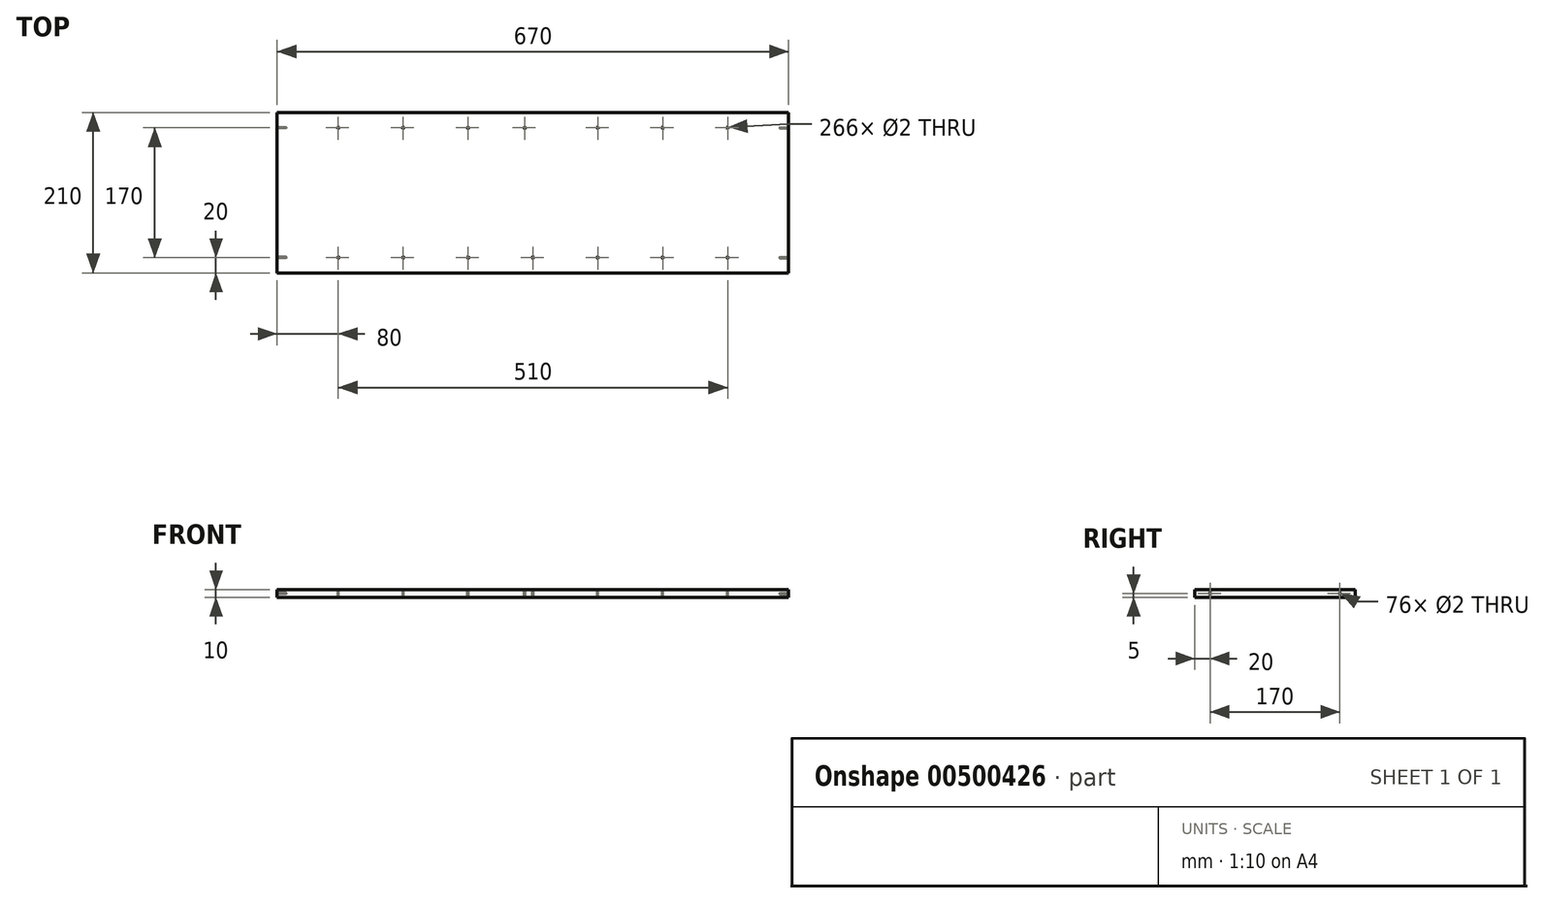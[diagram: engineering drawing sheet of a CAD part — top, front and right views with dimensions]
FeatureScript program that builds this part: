
annotation { "Feature Type Name" : "Feature", "Feature Type Description" : "" }
export const myFeature = defineFeature(function(context is Context, id is Id, definition is map)
    precondition{}
    {
        {
            var Q0;
            Q0=qCreatedBy(makeId("Top.planeOp"),FACE);
            var sketch = newSketch(context, id + "F0", { "sketchPlane" : qUnion([Q0])});
            skLineSegment(sketch, "E0.bottom", {"start": v(0, 0) * mm, "end": v(-670, 0) * mm});
            skLineSegment(sketch, "E0.top", {"start": v(0, -210) * mm, "end": v(-670, -210) * mm});
            skLineSegment(sketch, "E0.left", {"start": v(0, 0) * mm, "end": v(0, -210) * mm});
            skLineSegment(sketch, "E0.right", {"start": v(-670, 0) * mm, "end": v(-670, -210) * mm});
            skSolve(sketch);
        }
        {
            var Q0;
            Q0=makeQuery(id+"F0.imprint","IMPRINT",FACE,{"disambiguationData":[TD([[makeQuery(id+"F0.imprint","IMPRINT",EDGE,{"derivedFrom":sQuery(id+"F0.wireOp",EDGE,"E0.bottom")}),1.0]])]});
            extrude(context, id + "F1", {"entities" : qUnion([Q0]), "depth" : 10 * mm});
        }
        {
            var Q0;
            Q0=makeQuery(id+"F1.opExtrude","CAP_FACE",FACE,{"disambiguationData":[OSD([sQuery(id+"F0.wireOp",EDGE,"E0.bottom"),sQuery(id+"F0.wireOp",EDGE,"E0.top"),sQuery(id+"F0.wireOp",EDGE,"E0.left"),sQuery(id+"F0.wireOp",EDGE,"E0.right")])],"isStart":false});
            var sketch = newSketch(context, id + "F2", { "sketchPlane" : qUnion([Q0])});
            skPoint(sketch, "E1", {"position": v(-590, -190) * mm});
            skPoint(sketch, "E2", {"position": v(-505, -190) * mm});
            skPoint(sketch, "E3", {"position": v(-420, -190) * mm});
            skPoint(sketch, "E4", {"position": v(-335, -190) * mm});
            skPoint(sketch, "E5", {"position": v(-250, -190) * mm});
            skPoint(sketch, "E6", {"position": v(-165, -190) * mm});
            skPoint(sketch, "E7", {"position": v(-80, -190) * mm});
            skPoint(sketch, "E8", {"position": v(-590, -20) * mm});
            skPoint(sketch, "E9", {"position": v(-505, -20) * mm});
            skPoint(sketch, "E10", {"position": v(-420, -20) * mm});
            skPoint(sketch, "E11", {"position": v(-345.75, -20) * mm});
            skPoint(sketch, "E12", {"position": v(-250, -20) * mm});
            skPoint(sketch, "E13", {"position": v(-165, -20) * mm});
            skPoint(sketch, "E14", {"position": v(-80, -20) * mm});
            skSolve(sketch);
        }
        {
            var Q0;
            Q0=sQuery(id+"F2.wireOp",VERTEX,"E1");
            var Q1;
            Q1=sQuery(id+"F2.wireOp",VERTEX,"E2");
            var Q2;
            Q2=sQuery(id+"F2.wireOp",VERTEX,"E3");
            var Q3;
            Q3=sQuery(id+"F2.wireOp",VERTEX,"E4");
            var Q4;
            Q4=sQuery(id+"F2.wireOp",VERTEX,"E5");
            var Q5;
            Q5=sQuery(id+"F2.wireOp",VERTEX,"E6");
            var Q6;
            Q6=sQuery(id+"F2.wireOp",VERTEX,"E7");
            var Q7;
            Q7=sQuery(id+"F2.wireOp",VERTEX,"E14");
            var Q8;
            Q8=sQuery(id+"F2.wireOp",VERTEX,"E13");
            var Q9;
            Q9=sQuery(id+"F2.wireOp",VERTEX,"E12");
            var Q10;
            Q10=sQuery(id+"F2.wireOp",VERTEX,"E11");
            var Q11;
            Q11=sQuery(id+"F2.wireOp",VERTEX,"E10");
            var Q12;
            Q12=sQuery(id+"F2.wireOp",VERTEX,"E9");
            var Q13;
            Q13=sQuery(id+"F2.wireOp",VERTEX,"E8");
            var Q14;
            Q14=makeQuery(id+"F1.opExtrude","SWEPT_BODY",BODY,{"disambiguationData":[OSD([sQuery(id+"F0.wireOp",EDGE,"E0.bottom"),sQuery(id+"F0.wireOp",EDGE,"E0.top"),sQuery(id+"F0.wireOp",EDGE,"E0.left"),sQuery(id+"F0.wireOp",EDGE,"E0.right")])]});
            hole(context, id + "F3", {"style" : HoleStyle.SIMPLE, "endStyle" : HoleEndStyle.THROUGH, "holeDiameter" : 2 * mm, "isTappedThrough" : true, "tappedDepth" : 12 * mm, "tapClearance" : 3, "locations" : qUnion([Q0, Q1, Q2, Q3, Q4, Q5, Q6, Q7, Q8, Q9, Q10, Q11, Q12, Q13]), "scope" : qUnion([Q14])});
        }
        {
            var Q0;
            Q0=makeQuery(id+"F1.opExtrude","SWEPT_FACE",FACE,{"disambiguationData":[OSD([sQuery(id+"F0.wireOp",EDGE,"E0.left")])]});
            var sketch = newSketch(context, id + "F4", { "sketchPlane" : qUnion([Q0])});
            skPoint(sketch, "E15", {"position": v(-190, 5) * mm});
            skPoint(sketch, "E15.positionSnap0", {"position": v(-210, 5) * mm});
            skPoint(sketch, "E16", {"position": v(-20, 5) * mm});
            skSolve(sketch);
        }
        {
            var Q0;
            Q0=sQuery(id+"F4.wireOp",VERTEX,"E15");
            var Q1;
            Q1=sQuery(id+"F4.wireOp",VERTEX,"E16");
            var Q2;
            Q2=makeQuery(id+"F1.opExtrude","SWEPT_BODY",BODY,{"disambiguationData":[OSD([sQuery(id+"F0.wireOp",EDGE,"E0.bottom"),sQuery(id+"F0.wireOp",EDGE,"E0.top"),sQuery(id+"F0.wireOp",EDGE,"E0.left"),sQuery(id+"F0.wireOp",EDGE,"E0.right")])]});
            hole(context, id + "F5", {"style" : HoleStyle.SIMPLE, "endStyle" : HoleEndStyle.BLIND, "holeDiameter" : 2 * mm, "holeDepth" : 12 * mm, "isTappedThrough" : true, "tappedDepth" : 12 * mm, "tapClearance" : 3, "locations" : qUnion([Q0, Q1]), "scope" : qUnion([Q2])});
        }
        {
            var Q0;
            Q0=makeQuery(id+"F1.opExtrude","SWEPT_FACE",FACE,{"disambiguationData":[OSD([sQuery(id+"F0.wireOp",EDGE,"E0.right")])]});
            var sketch = newSketch(context, id + "F6", { "sketchPlane" : qUnion([Q0])});
            skPoint(sketch, "E17", {"position": v(20, 5) * mm});
            skPoint(sketch, "E17.positionSnap0", {"position": v(0, 5) * mm});
            skPoint(sketch, "E18", {"position": v(190, 5) * mm});
            skSolve(sketch);
        }
        {
            var Q0;
            Q0=sQuery(id+"F6.wireOp",VERTEX,"E17");
            var Q1;
            Q1=sQuery(id+"F6.wireOp",VERTEX,"E18");
            var Q2;
            Q2=makeQuery(id+"F1.opExtrude","SWEPT_BODY",BODY,{"disambiguationData":[OSD([sQuery(id+"F0.wireOp",EDGE,"E0.bottom"),sQuery(id+"F0.wireOp",EDGE,"E0.top"),sQuery(id+"F0.wireOp",EDGE,"E0.left"),sQuery(id+"F0.wireOp",EDGE,"E0.right")])]});
            hole(context, id + "F7", {"style" : HoleStyle.SIMPLE, "endStyle" : HoleEndStyle.BLIND, "holeDiameter" : 2 * mm, "holeDepth" : 12 * mm, "isTappedThrough" : true, "tappedDepth" : 12 * mm, "tapClearance" : 3, "locations" : qUnion([Q0, Q1]), "scope" : qUnion([Q2])});
        }
    });
